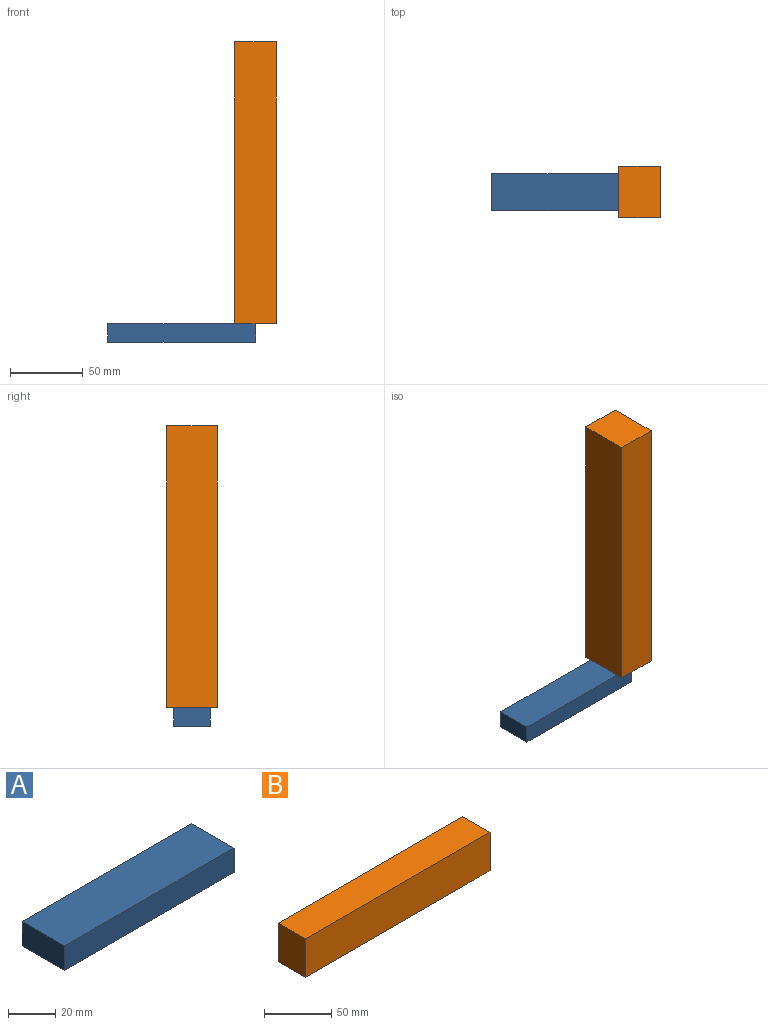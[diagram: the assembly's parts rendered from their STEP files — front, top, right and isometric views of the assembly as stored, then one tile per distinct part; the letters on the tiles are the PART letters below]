
ASSEMBLY  parts=2 mates=1
PART A: 6 faces, bbox 101.6x25.4x12.7 mm
  f0: plane 25.4x12.7mm, normal (1,0,0), area 322.6mm2, adj f1,f3,f4,f5
  f1: plane 101.6x25.4mm, normal (0,0,1), area 2580.6mm2, adj f0,f2,f4,f5
  f2: plane 25.4x12.7mm, normal (-1,0,0), area 322.6mm2, adj f1,f3,f4,f5
  f3: plane 101.6x25.4mm, normal (0,0,-1), area 2580.6mm2, adj f0,f2,f4,f5
  f4: plane 101.6x12.7mm, normal (0,-1,0), area 1290.3mm2, adj f0,f1,f2,f3
  f5: plane 101.6x12.7mm, normal (0,1,0), area 1290.3mm2, adj f0,f1,f2,f3
PART B: 6 faces, bbox 193.7x28.6x34.9 mm
  f0: plane 193.68x28.58mm, normal (0,0,1), area 5534.3mm2, adj f1,f3,f4,f5
  f1: plane 34.93x28.58mm, normal (-1,0,0), area 998mm2, adj f0,f2,f4,f5
  f2: plane 193.68x28.58mm, normal (0,0,-1), area 5534.3mm2, adj f1,f3,f4,f5
  f3: plane 34.93x28.58mm, normal (1,0,0), area 998mm2, adj f0,f2,f4,f5
  f4: plane 193.68x34.93mm, normal (0,-1,0), area 6764.1mm2, adj f0,f1,f2,f3
  f5: plane 193.68x34.93mm, normal (0,1,0), area 6764.1mm2, adj f0,f1,f2,f3
PLACE A t=(206.07,69.56,-28.2)mm
PLACE B rot(axis=(0.58,0.58,-0.58),120deg) t=(220.35,39.4,165.47)mm
MATE fastened B.f3 <-> A.f1  axis (0,0,-1) through (206.07,56.86,-28.2)mm
